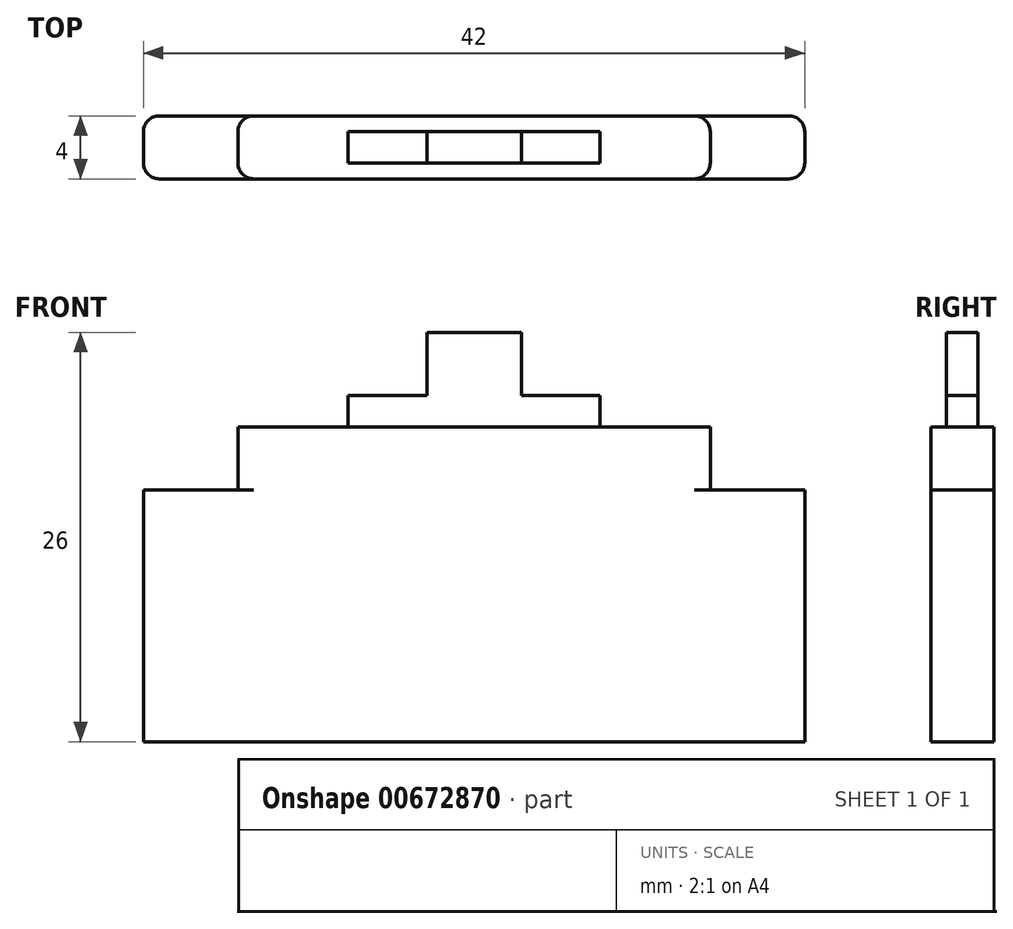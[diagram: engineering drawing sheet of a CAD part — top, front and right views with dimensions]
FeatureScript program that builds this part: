
annotation { "Feature Type Name" : "Feature", "Feature Type Description" : "" }
export const myFeature = defineFeature(function(context is Context, id is Id, definition is map)
    precondition{}
    {
        {
            var Q0;
            Q0=qCreatedBy(makeId("Top.planeOp"),FACE);
            var sketch = newSketch(context, id + "F0", { "sketchPlane" : qUnion([Q0])});
            skLineSegment(sketch, "E0.bottom", {"start": v(3, -1) * mm, "end": v(-3, -1) * mm});
            skLineSegment(sketch, "E0.top", {"start": v(3, 1) * mm, "end": v(-3, 1) * mm});
            skLineSegment(sketch, "E0.left", {"start": v(3, -1) * mm, "end": v(3, 1) * mm});
            skLineSegment(sketch, "E0.right", {"start": v(-3, -1) * mm, "end": v(-3, 1) * mm});
            skPoint(sketch, "E0.middle", {"position": v(0, 0) * mm});
            skLineSegment(sketch, "E1.bottom", {"start": v(8, -1) * mm, "end": v(-8, -1) * mm});
            skLineSegment(sketch, "E1.top", {"start": v(8, 1) * mm, "end": v(-8, 1) * mm});
            skLineSegment(sketch, "E1.left", {"start": v(8, -1) * mm, "end": v(8, 1) * mm});
            skLineSegment(sketch, "E1.right", {"start": v(-8, -1) * mm, "end": v(-8, 1) * mm});
            skLineSegment(sketch, "E2.bottom", {"start": v(20, -2) * mm, "end": v(-20, -2) * mm});
            skLineSegment(sketch, "E2.top", {"start": v(20, 2) * mm, "end": v(-20, 2) * mm});
            skLineSegment(sketch, "E2.left", {"start": v(21, -1) * mm, "end": v(21, 1) * mm});
            skLineSegment(sketch, "E2.right", {"start": v(-21, -1) * mm, "end": v(-21, 1) * mm});
            skPoint(sketch, "E3.visualSharp", {"position": v(-21, 2) * mm});
            skArc(sketch, "E3.filletArc", {"start": v(-20, 2) * mm, "mid": v(-20.7, 1.7) * mm, "end": v(-21, 1) * mm});
            skPoint(sketch, "E4.visualSharp", {"position": v(-21, -2) * mm});
            skArc(sketch, "E4.filletArc", {"start": v(-21, -1) * mm, "mid": v(-20.7, -1.7) * mm, "end": v(-20, -2) * mm});
            skPoint(sketch, "E5.visualSharp", {"position": v(21, -2) * mm});
            skArc(sketch, "E5.filletArc", {"start": v(20, -2) * mm, "mid": v(20.7, -1.7) * mm, "end": v(21, -1) * mm});
            skPoint(sketch, "E6.visualSharp", {"position": v(21, 2) * mm});
            skArc(sketch, "E6.filletArc", {"start": v(21, 1) * mm, "mid": v(20.7, 1.7) * mm, "end": v(20, 2) * mm});
            skLineSegment(sketch, "E7.bottom", {"start": v(14, -2) * mm, "end": v(-14, -2) * mm});
            skLineSegment(sketch, "E7.top", {"start": v(14, 2) * mm, "end": v(-14, 2) * mm});
            skLineSegment(sketch, "E7.left", {"start": v(15, -1) * mm, "end": v(15, 1) * mm});
            skLineSegment(sketch, "E7.right", {"start": v(-15, -1) * mm, "end": v(-15, 1) * mm});
            skPoint(sketch, "E8.visualSharp", {"position": v(-15, 2) * mm});
            skArc(sketch, "E8.filletArc", {"start": v(-14, 2) * mm, "mid": v(-14.7, 1.7) * mm, "end": v(-15, 1) * mm});
            skPoint(sketch, "E9.visualSharp", {"position": v(-15, -2) * mm});
            skArc(sketch, "E9.filletArc", {"start": v(-15, -1) * mm, "mid": v(-14.7, -1.7) * mm, "end": v(-14, -2) * mm});
            skPoint(sketch, "E10.visualSharp", {"position": v(15, -2) * mm});
            skArc(sketch, "E10.filletArc", {"start": v(14, -2) * mm, "mid": v(14.7, -1.7) * mm, "end": v(15, -1) * mm});
            skPoint(sketch, "E11.visualSharp", {"position": v(15, 2) * mm});
            skArc(sketch, "E11.filletArc", {"start": v(15, 1) * mm, "mid": v(14.7, 1.7) * mm, "end": v(14, 2) * mm});
            skSolve(sketch);
        }
        {
            var Q0;
            Q0=makeQuery(id+"F0.imprint","IMPRINT",FACE,{"disambiguationData":[TD([[makeQuery(id+"F0.imprint","IMPRINT",EDGE,{"derivedFrom":sQuery(id+"F0.wireOp",EDGE,"E2.right")}),-1.0]])]});
            var Q1;
            {var subQ1=sQuery(id+"F0.wireOp",EDGE,"E1.left");Q1=makeQuery(id+"F0.imprint","IMPRINT",FACE,{"disambiguationData":[TD([[makeQuery(id+"F0.imprint","IMPRINT",EDGE,{"derivedFrom":subQ1}),-1.0]])]});}
            var Q2;
            {var subQ0=sQuery(id+"F0.wireOp",EDGE,"E0.right");Q2=makeQuery(id+"F0.imprint","IMPRINT",FACE,{"disambiguationData":[TD([[makeQuery(id+"F0.imprint","IMPRINT",EDGE,{"derivedFrom":subQ0}),1.0]])]});}
            var Q3;
            {var subQ0=sQuery(id+"F0.wireOp",EDGE,"E0.left");Q3=makeQuery(id+"F0.imprint","IMPRINT",FACE,{"disambiguationData":[TD([[makeQuery(id+"F0.imprint","IMPRINT",EDGE,{"derivedFrom":subQ0}),1.0]])]});}
            var Q4;
            {var subQ0=sQuery(id+"F0.wireOp",EDGE,"E0.left");Q4=makeQuery(id+"F0.imprint","IMPRINT",FACE,{"disambiguationData":[TD([[makeQuery(id+"F0.imprint","IMPRINT",EDGE,{"derivedFrom":subQ0}),-1.0]])]});}
            var Q5;
            Q5=makeQuery(id+"F0.imprint","IMPRINT",FACE,{"disambiguationData":[TD([[makeQuery(id+"F0.imprint","IMPRINT",EDGE,{"derivedFrom":sQuery(id+"F0.wireOp",EDGE,"E2.left")}),1.0]])]});
            extrude(context, id + "F1", {"entities" : qUnion([Q0, Q1, Q2, Q3, Q4, Q5]), "oppositeDirection" : true, "depth" : 16 * mm, "offsetDistance" : 25 * mm});
        }
        {
            var Q0;
            {var subQ1=sQuery(id+"F0.wireOp",EDGE,"E1.left");Q0=makeQuery(id+"F0.imprint","IMPRINT",FACE,{"disambiguationData":[TD([[makeQuery(id+"F0.imprint","IMPRINT",EDGE,{"derivedFrom":subQ1}),-1.0]])]});}
            extrude(context, id + "F2", {"entities" : qUnion([Q0]), "operationType" : NewBodyOperationType.ADD, "depth" : 4 * mm, "offsetDistance" : 25 * mm});
        }
        {
            var Q0;
            {var subQ0=sQuery(id+"F0.wireOp",EDGE,"E0.right");Q0=makeQuery(id+"F0.imprint","IMPRINT",FACE,{"disambiguationData":[TD([[makeQuery(id+"F0.imprint","IMPRINT",EDGE,{"derivedFrom":subQ0}),1.0]])]});}
            var Q1;
            {var subQ0=sQuery(id+"F0.wireOp",EDGE,"E0.left");Q1=makeQuery(id+"F0.imprint","IMPRINT",FACE,{"disambiguationData":[TD([[makeQuery(id+"F0.imprint","IMPRINT",EDGE,{"derivedFrom":subQ0}),-1.0]])]});}
            extrude(context, id + "F3", {"entities" : qUnion([Q0, Q1]), "operationType" : NewBodyOperationType.ADD, "depth" : 6 * mm, "offsetDistance" : 25 * mm});
        }
        {
            var Q0;
            {var subQ0=sQuery(id+"F0.wireOp",EDGE,"E0.left");Q0=makeQuery(id+"F0.imprint","IMPRINT",FACE,{"disambiguationData":[TD([[makeQuery(id+"F0.imprint","IMPRINT",EDGE,{"derivedFrom":subQ0}),1.0]])]});}
            extrude(context, id + "F4", {"entities" : qUnion([Q0]), "operationType" : NewBodyOperationType.ADD, "depth" : 10 * mm, "offsetDistance" : 25 * mm});
        }
    });
